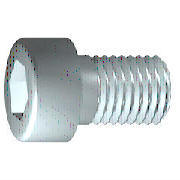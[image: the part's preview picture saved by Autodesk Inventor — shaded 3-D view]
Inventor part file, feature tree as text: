
AUTODESK INVENTOR PART (.ipt)
format: ipt  version: 2023.3 (Build 273359000, 359)  size: 187,904 bytes
history: native  units: mm (DEFAULTED — no unit token found)
features: sketch x2, other x1, extrude x1, plane x1, fillet x1
ambient origin geometry x7: Origin, YZ Plane, XY Plane, X Axis, Y Axis, Z Axis, Center Point
bodies: Solid1 (feature_tree)
feature tree (6):
  other  "Körper"
  extrude  "Loch"  Depth=2.5mm
  plane  "Work Plane1"
  fillet  "Fillet2"  Radius=2.5mm
  sketch  "Skizze1"  dims[d1=14.875mm d2=0.276153mm d3=2.5mm]
  sketch  "Skizze2"  dims[d4=1.1mm d5=60.0deg d6=2.5mm d7=2.5mm d8=2.309401mm d9=4.5mm d10=90.0deg d11=10.0mm d12=0.0mm d13=14.875mm d14=0.0mm d15=0.276052mm d16=0.276053mm d17=0.25mm d19=0.0mm d26=16.0mm d27=45.0deg d28=0.0mm d29=0.0mm d30=0.1mm]
